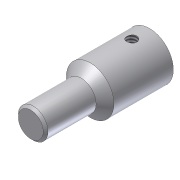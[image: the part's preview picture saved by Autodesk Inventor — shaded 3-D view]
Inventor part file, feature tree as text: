
AUTODESK INVENTOR PART (.ipt)
format: ipt  version: unknown  size: 192,000 bytes
history: native  units: in
note: dims shown in document units (in); Inventor stores cm internally (conversion verified against a paired STEP export)
features: sketch x5, extrude x3, chamfer x2, plane x1, hole x1
ambient origin geometry x8: Origin, YZ Plane, XZ Plane, XY Plane, X Axis, Y Axis, Z Axis, Center Point
feature tree (12):
  extrude  "Extrusion1"  Depth=1.0in TaperAngle=0.0deg
  extrude  "Extrusion2"  Depth=0.5in TaperAngle=0.0deg
  extrude  "Extrusion3"  Depth=0.5in TaperAngle=0.0deg
  sketch  "Sketch4"  dims[d9=0.15in]
  plane  "Work Plane1"
  hole  "Hole1"  [1 undecoded]
  chamfer  "Chamfer1"  Distance=0.02in Angle=45.0deg
  chamfer  "Chamfer2"  [1 undecoded]
  sketch  "Sketch1"  dims[d0=0.4in d1=1.0in d2=0.0in]
  sketch  "Sketch2"  dims[d3=0.25in d4=0.5in d5=0.0in]
  sketch  "Sketch3"  dims[d6=0.198in d7=0.5in d8=0.0in]
  sketch  "Sketch5"  dims[d10=0.085in d11=0.5in d12=0.375in d13=0.25in d14=0.5635in d15=0.75in d16=0.8108in d17=0.075in d18=0.125in d19=45.0deg d20=0.02in d21=0.125in d22=45.0deg]
note: 2 required parameter values undecoded (feature->parameter linkage not recoverable at this tier; creation-order binding heuristic only, values carry confidence <= 0.55)
